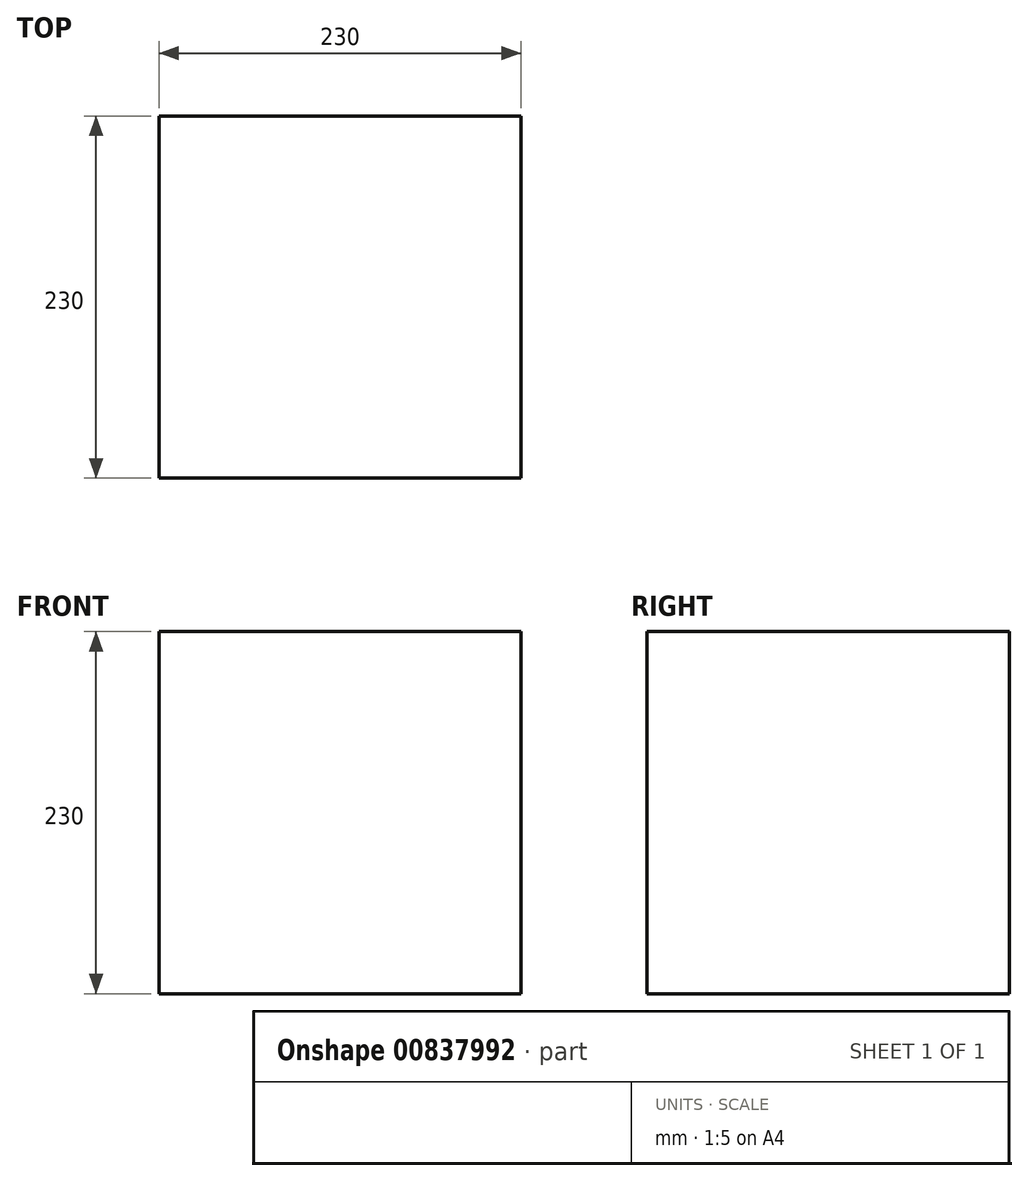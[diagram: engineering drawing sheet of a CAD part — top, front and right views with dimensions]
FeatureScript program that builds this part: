
annotation { "Feature Type Name" : "Feature", "Feature Type Description" : "" }
export const myFeature = defineFeature(function(context is Context, id is Id, definition is map)
    precondition{}
    {
        {
            var Q0;
            Q0=qCreatedBy(makeId("Top.planeOp"),FACE);
            var sketch = newSketch(context, id + "F0", { "sketchPlane" : qUnion([Q0])});
            skLineSegment(sketch, "E0.bottom", {"start": v(-1048.81, 112) * mm, "end": v(-818.81, 112) * mm});
            skLineSegment(sketch, "E0.top", {"start": v(-1048.81, -118) * mm, "end": v(-818.81, -118) * mm});
            skLineSegment(sketch, "E0.left", {"start": v(-1048.81, 112) * mm, "end": v(-1048.81, -118) * mm});
            skLineSegment(sketch, "E0.right", {"start": v(-818.81, 112) * mm, "end": v(-818.81, -118) * mm});
            skSolve(sketch);
        }
        {
            var Q0;
            Q0=makeQuery(id+"F0.imprint","IMPRINT",FACE,{"disambiguationData":[TD([[makeQuery(id+"F0.imprint","IMPRINT",EDGE,{"derivedFrom":sQuery(id+"F0.wireOp",EDGE,"E0.bottom")}),-1.0]])]});
            extrude(context, id + "F1", {"entities" : qUnion([Q0]), "depth" : 230 * mm, "offsetDistance" : 25 * mm});
        }
    });
